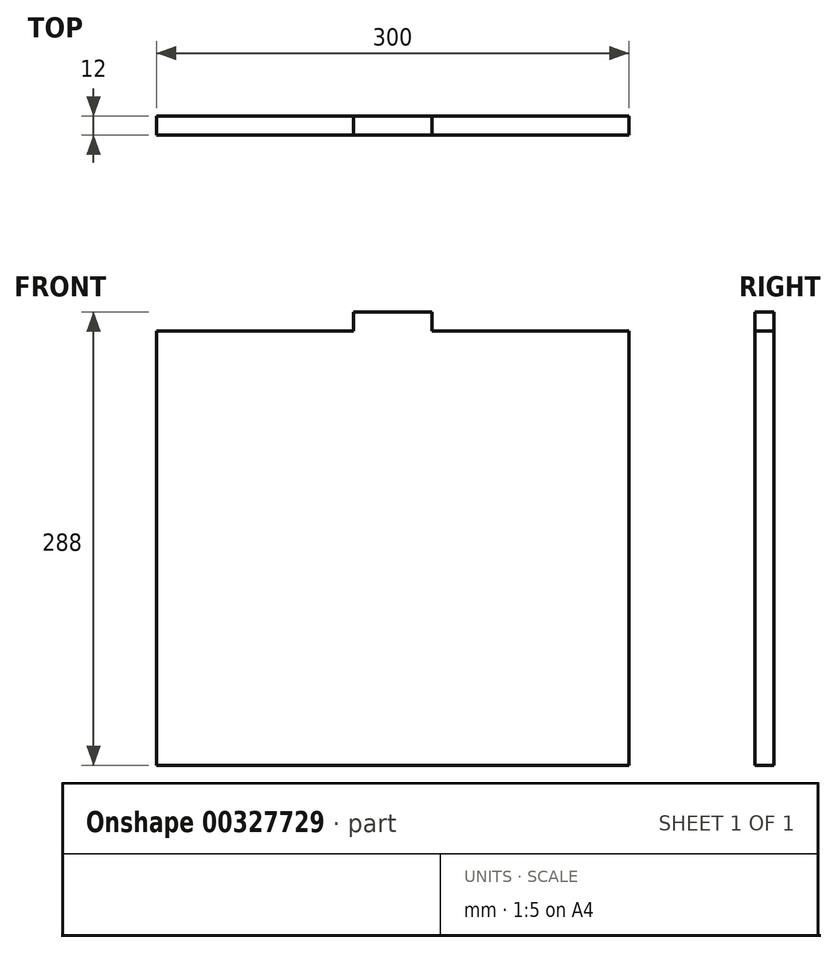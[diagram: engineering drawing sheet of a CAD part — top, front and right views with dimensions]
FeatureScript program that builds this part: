
annotation { "Feature Type Name" : "Feature", "Feature Type Description" : "" }
export const myFeature = defineFeature(function(context is Context, id is Id, definition is map)
    precondition{}
    {
        {
            var Q0;
            Q0=qCreatedBy(makeId("Front.planeOp"),FACE);
            var sketch = newSketch(context, id + "F0", { "sketchPlane" : qUnion([Q0])});
            skLineSegment(sketch, "E0", {"start": v(-57.2, 164.93) * mm, "end": v(-57.2, 152.93) * mm});
            skLineSegment(sketch, "E1", {"start": v(-7.2, 152.93) * mm, "end": v(-7.2, 164.93) * mm});
            skLineSegment(sketch, "E2", {"start": v(-57.2, 164.93) * mm, "end": v(-7.2, 164.93) * mm});
            skLineSegment(sketch, "E3", {"start": v(-57.2, 152.93) * mm, "end": v(-182.2, 152.93) * mm});
            skLineSegment(sketch, "E4", {"start": v(-7.2, 152.93) * mm, "end": v(117.8, 152.93) * mm});
            skLineSegment(sketch, "E5", {"start": v(-182.2, -123.07) * mm, "end": v(117.8, -123.07) * mm});
            skLineSegment(sketch, "E6", {"start": v(-182.2, 152.93) * mm, "end": v(-182.2, -123.07) * mm});
            skLineSegment(sketch, "E7", {"start": v(117.8, 152.93) * mm, "end": v(117.8, -123.07) * mm});
            skSolve(sketch);
        }
        {
            var Q0;
            Q0 = qSketchRegion(id + "F0", true);
            extrude(context, id + "F1", {"entities" : qUnion([Q0]), "depth" : 12 * mm});
        }
    });
